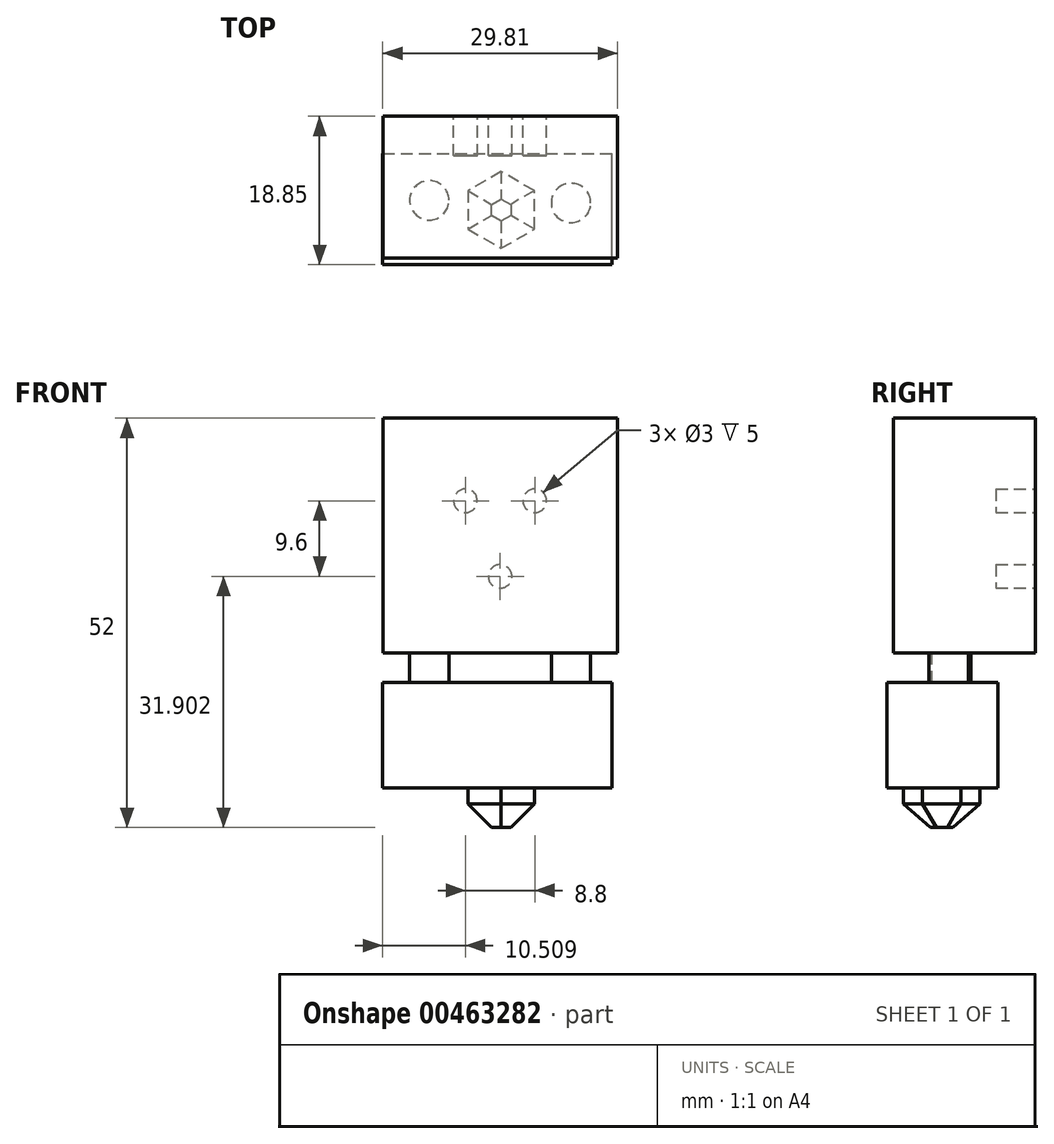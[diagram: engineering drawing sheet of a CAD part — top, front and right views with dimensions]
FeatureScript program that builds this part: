
annotation { "Feature Type Name" : "Feature", "Feature Type Description" : "" }
export const myFeature = defineFeature(function(context is Context, id is Id, definition is map)
    precondition{}
    {
        {
            var Q0;
            Q0=qCreatedBy(makeId("Front.planeOp"),FACE);
            var sketch = newSketch(context, id + "F0", { "sketchPlane" : qUnion([Q0])});
            skLineSegment(sketch, "E0.bottom", {"start": v(-29.1, 53.17) * mm, "end": v(0.7, 53.17) * mm});
            skLineSegment(sketch, "E0.top", {"start": v(-29.1, 23.37) * mm, "end": v(0.7, 23.37) * mm});
            skLineSegment(sketch, "E0.left", {"start": v(-29.1, 53.17) * mm, "end": v(-29.1, 23.37) * mm});
            skLineSegment(sketch, "E0.right", {"start": v(0.7, 53.17) * mm, "end": v(0.7, 23.37) * mm});
            skSolve(sketch);
        }
        {
            var Q0;
            Q0=makeQuery(id+"F0.imprint","IMPRINT",FACE,{"disambiguationData":[TD([[makeQuery(id+"F0.imprint","IMPRINT",EDGE,{"derivedFrom":sQuery(id+"F0.wireOp",EDGE,"E0.bottom")}),-1.0]])]});
            extrude(context, id + "F1", {"entities" : qUnion([Q0]), "depth" : 18 * mm});
        }
        {
            var Q0;
            Q0=makeQuery(id+"F1.opExtrude","SWEPT_FACE",FACE,{"disambiguationData":[OSD([sQuery(id+"F0.wireOp",EDGE,"E0.top")])]});
            var sketch = newSketch(context, id + "F2", { "sketchPlane" : qUnion([Q0])});
            skCircle(sketch, "E1", {"center": v(-23.2, 10.67) * mm, "radius": 2.5 * mm});
            skCircle(sketch, "E2", {"center": v(-5.2, 11.01) * mm, "radius": 2.5 * mm});
            skLineSegment(sketch, "E3", {"start": v(-14.2, 29.51) * mm, "end": v(-14.2, -25.47) * mm, "construction": true});
            skSolve(sketch);
        }
        {
            var Q0;
            Q0=makeQuery(id+"F2.imprint","IMPRINT",FACE,{"disambiguationData":[TD([[makeQuery(id+"F2.imprint","IMPRINT",EDGE,{"derivedFrom":sQuery(id+"F2.wireOp",EDGE,"E2")}),1.0]])]});
            var Q1;
            Q1=makeQuery(id+"F2.imprint","IMPRINT",FACE,{"disambiguationData":[TD([[makeQuery(id+"F2.imprint","IMPRINT",EDGE,{"derivedFrom":sQuery(id+"F2.wireOp",EDGE,"E1")}),1.0]])]});
            extrude(context, id + "F3", {"entities" : qUnion([Q0, Q1]), "depth" : 3.8 * mm});
        }
        {
            var Q0;
            Q0=makeQuery(id+"F3.opExtrude","CAP_FACE",FACE,{"disambiguationData":[OSD([sQuery(id+"F2.wireOp",EDGE,"E1")])],"isStart":false});
            var sketch = newSketch(context, id + "F4", { "sketchPlane" : qUnion([Q0])});
            skLineSegment(sketch, "E4.bottom", {"start": v(-29.1, 18.85) * mm, "end": v(0, 18.85) * mm});
            skLineSegment(sketch, "E4.top", {"start": v(-29.1, 4.75) * mm, "end": v(0, 4.75) * mm});
            skLineSegment(sketch, "E4.left", {"start": v(-29.1, 18.85) * mm, "end": v(-29.1, 4.75) * mm});
            skLineSegment(sketch, "E4.right", {"start": v(0, 18.85) * mm, "end": v(0, 4.75) * mm});
            skPoint(sketch, "E5.startSnap0", {"position": v(-14.55, 18.85) * mm});
            skSolve(sketch);
        }
        {
            var Q0;
            Q0=makeQuery(id+"F4.imprint","IMPRINT",FACE,{"disambiguationData":[TD([[makeQuery(id+"F4.imprint","IMPRINT",EDGE,{"derivedFrom":makeQuery(id+"F3.opExtrude","CAP_EDGE",EDGE,{"disambiguationData":[OSD([sQuery(id+"F2.wireOp",EDGE,"E1")])],"isStart":false})}),1.0]])]});
            var Q1;
            Q1=makeQuery(id+"F4.imprint","IMPRINT",FACE,{"disambiguationData":[TD([[makeQuery(id+"F4.imprint","IMPRINT",EDGE,{"derivedFrom":sQuery(id+"F4.wireOp",EDGE,"E4.bottom")}),-1.0]])]});
            extrude(context, id + "F5", {"entities" : qUnion([Q0, Q1]), "operationType" : NewBodyOperationType.ADD, "depth" : 13.4 * mm});
        }
        {
            var Q0;
            Q0=makeQuery(id+"F1.opExtrude","CAP_FACE",FACE,{"disambiguationData":[OSD([sQuery(id+"F0.wireOp",EDGE,"E0.bottom"),sQuery(id+"F0.wireOp",EDGE,"E0.top"),sQuery(id+"F0.wireOp",EDGE,"E0.left"),sQuery(id+"F0.wireOp",EDGE,"E0.right")])],"isStart":true});
            var sketch = newSketch(context, id + "F6", { "sketchPlane" : qUnion([Q0])});
            skCircle(sketch, "E6", {"center": v(9.8, 42.67) * mm, "radius": 1.5 * mm});
            skCircle(sketch, "E7", {"center": v(18.6, 42.67) * mm, "radius": 1.5 * mm});
            skCircle(sketch, "E8", {"center": v(14.2, 33.07) * mm, "radius": 1.5 * mm});
            skSolve(sketch);
        }
        {
            var Q0;
            Q0=makeQuery(id+"F6.imprint","IMPRINT",FACE,{"disambiguationData":[TD([[makeQuery(id+"F6.imprint","IMPRINT",EDGE,{"derivedFrom":sQuery(id+"F6.wireOp",EDGE,"E6")}),1.0]])]});
            var Q1;
            Q1=makeQuery(id+"F6.imprint","IMPRINT",FACE,{"disambiguationData":[TD([[makeQuery(id+"F6.imprint","IMPRINT",EDGE,{"derivedFrom":sQuery(id+"F6.wireOp",EDGE,"E7")}),1.0]])]});
            var Q2;
            Q2=makeQuery(id+"F6.imprint","IMPRINT",FACE,{"disambiguationData":[TD([[makeQuery(id+"F6.imprint","IMPRINT",EDGE,{"derivedFrom":sQuery(id+"F6.wireOp",EDGE,"E8")}),1.0]])]});
            extrude(context, id + "F7", {"entities" : qUnion([Q0, Q1, Q2]), "operationType" : NewBodyOperationType.REMOVE, "oppositeDirection" : true, "depth" : 5 * mm});
        }
        {
            var Q0;
            Q0=makeQuery(id+"F5.opExtrude","CAP_FACE",FACE,{"disambiguationData":[OSD([sQuery(id+"F4.wireOp",EDGE,"E4.bottom"),sQuery(id+"F4.wireOp",EDGE,"E4.top"),sQuery(id+"F4.wireOp",EDGE,"E4.left"),sQuery(id+"F4.wireOp",EDGE,"E4.right")])],"isStart":false});
            var sketch = newSketch(context, id + "F8", { "sketchPlane" : qUnion([Q0])});
            skCircle(sketch, "E9.cCircle", {"center": v(-14.06, 11.9) * mm, "radius": 4.22 * mm, "construction": true});
            skLineSegment(sketch, "E9.0", {"start": v(-18.28, 9.46) * mm, "end": v(-18.28, 14.33) * mm});
            skLineSegment(sketch, "E9.1", {"start": v(-18.28, 14.33) * mm, "end": v(-14.06, 16.77) * mm});
            skLineSegment(sketch, "E9.2", {"start": v(-14.06, 16.77) * mm, "end": v(-9.84, 14.33) * mm});
            skLineSegment(sketch, "E9.3", {"start": v(-9.84, 14.33) * mm, "end": v(-9.84, 9.46) * mm});
            skLineSegment(sketch, "E9.4", {"start": v(-9.84, 9.46) * mm, "end": v(-14.06, 7.02) * mm});
            skLineSegment(sketch, "E9.5", {"start": v(-14.06, 7.02) * mm, "end": v(-18.28, 9.46) * mm});
            skPoint(sketch, "E9.0.midPoint", {"position": v(-18.28, 11.9) * mm});
            skSolve(sketch);
        }
        {
            var Q0;
            Q0 = qSketchRegion(id + "F8", true);
            extrude(context, id + "F9", {"entities" : qUnion([Q0]), "operationType" : NewBodyOperationType.ADD, "depth" : 5 * mm});
        }
        {
            var Q0;
            Q0=makeQuery(id+"F9.opExtrude","CAP_EDGE",EDGE,{"disambiguationData":[OSD([sQuery(id+"F8.wireOp",EDGE,"E9.2")])],"isStart":false});
            var Q1;
            Q1=makeQuery(id+"F9.opExtrude","CAP_EDGE",EDGE,{"disambiguationData":[OSD([sQuery(id+"F8.wireOp",EDGE,"E9.0")])],"isStart":false});
            var Q2;
            Q2=makeQuery(id+"F9.opExtrude","CAP_EDGE",EDGE,{"disambiguationData":[OSD([sQuery(id+"F8.wireOp",EDGE,"E9.1")])],"isStart":false});
            var Q3;
            Q3=makeQuery(id+"F9.opExtrude","CAP_EDGE",EDGE,{"disambiguationData":[OSD([sQuery(id+"F8.wireOp",EDGE,"E9.5")])],"isStart":false});
            var Q4;
            Q4=makeQuery(id+"F9.opExtrude","CAP_EDGE",EDGE,{"disambiguationData":[OSD([sQuery(id+"F8.wireOp",EDGE,"E9.4")])],"isStart":false});
            var Q5;
            Q5=makeQuery(id+"F9.opExtrude","CAP_EDGE",EDGE,{"disambiguationData":[OSD([sQuery(id+"F8.wireOp",EDGE,"E9.3")])],"isStart":false});
            chamfer(context, id + "F10", {"entities" : qUnion([Q0, Q1, Q2, Q3, Q4, Q5]), "width" : 3 * mm, "tangentPropagation" : true});
        }
    });
